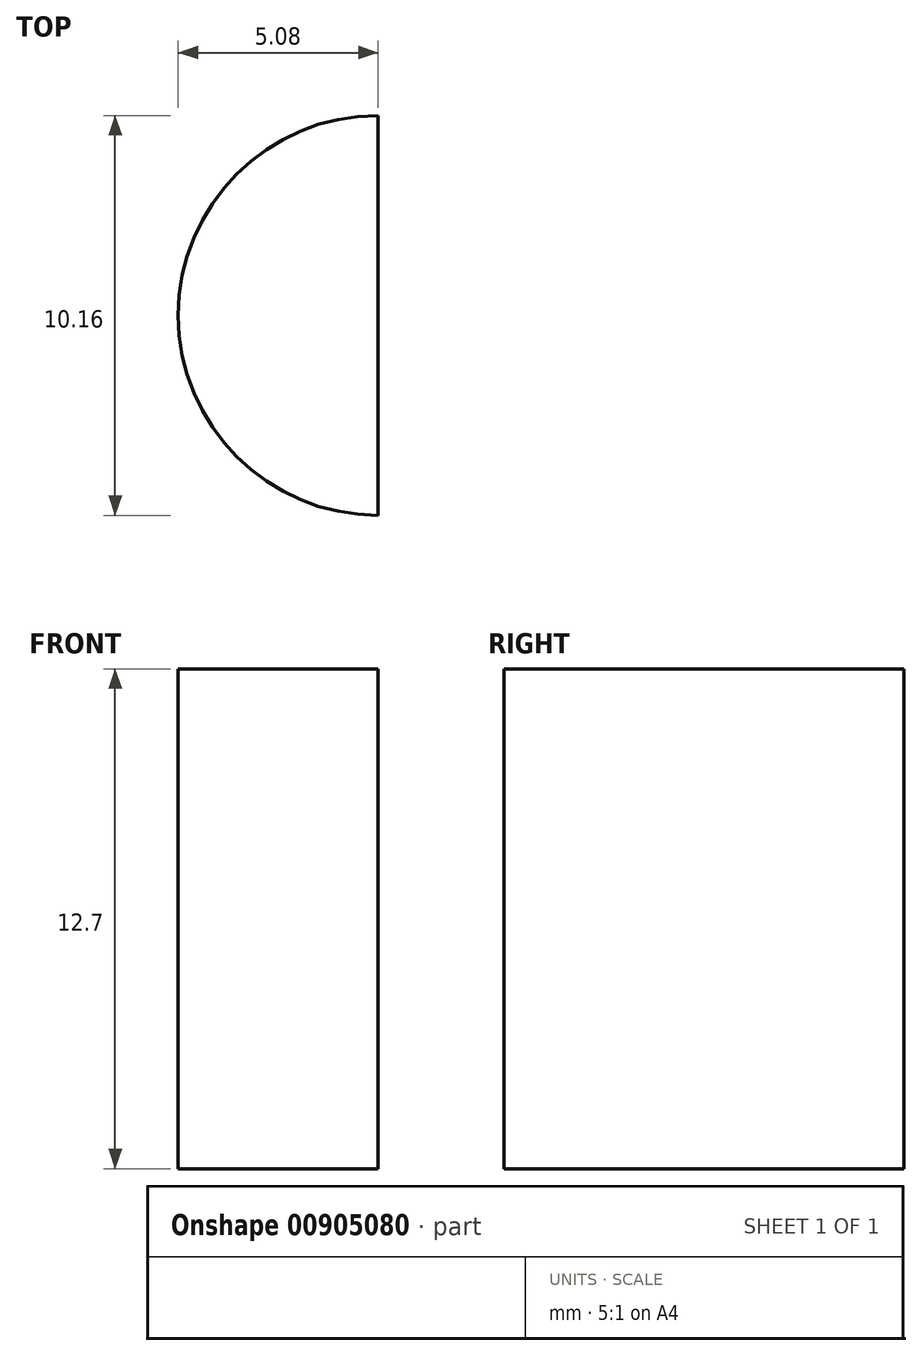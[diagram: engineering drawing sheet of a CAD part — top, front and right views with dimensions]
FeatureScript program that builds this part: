
annotation { "Feature Type Name" : "Feature", "Feature Type Description" : "" }
export const myFeature = defineFeature(function(context is Context, id is Id, definition is map)
    precondition{}
    {
        {
            var Q0;
            Q0=qCreatedBy(makeId("Top.planeOp"),FACE);
            var sketch = newSketch(context, id + "F0", { "sketchPlane" : qUnion([Q0])});
            skArc(sketch, "E0", {"start": v(0, 5.08) * mm, "mid": v(-5.08, 0) * mm, "end": v(0, -5.08) * mm});
            skLineSegment(sketch, "E1", {"start": v(0, -5.08) * mm, "end": v(0, 5.08) * mm});
            skSolve(sketch);
        }
        {
            var Q0;
            Q0 = qSketchRegion(id + "F0", true);
            extrude(context, id + "F1", {"entities" : qUnion([Q0]), "depth" : 12.7 * mm, "offsetDistance" : 25.4 * mm});
        }
    });
